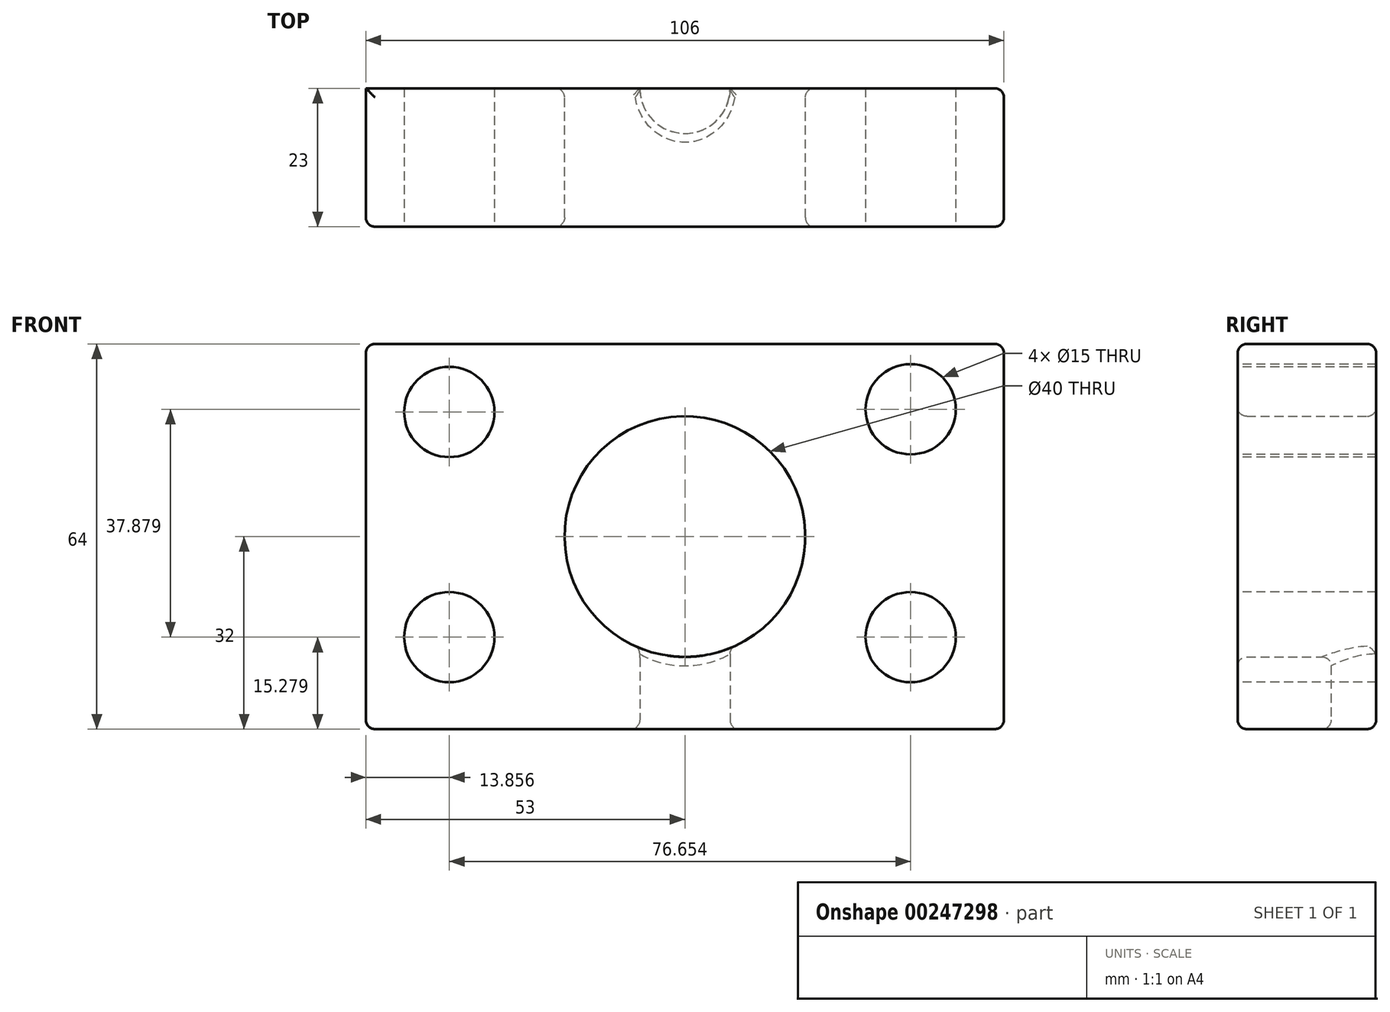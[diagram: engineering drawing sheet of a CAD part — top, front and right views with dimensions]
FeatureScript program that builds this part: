
annotation { "Feature Type Name" : "Feature", "Feature Type Description" : "" }
export const myFeature = defineFeature(function(context is Context, id is Id, definition is map)
    precondition{}
    {
        {
            var Q0;
            Q0=qCreatedBy(makeId("Front.planeOp"),FACE);
            var sketch = newSketch(context, id + "F0", { "sketchPlane" : qUnion([Q0])});
            skCircle(sketch, "E0", {"center": v(0, 0) * mm, "radius": 20 * mm});
            skLineSegment(sketch, "E1.bottom", {"start": v(-53, 32) * mm, "end": v(53, 32) * mm});
            skLineSegment(sketch, "E1.top", {"start": v(-53, -32) * mm, "end": v(53, -32) * mm});
            skLineSegment(sketch, "E1.left", {"start": v(-53, 32) * mm, "end": v(-53, -32) * mm});
            skLineSegment(sketch, "E1.right", {"start": v(53, 32) * mm, "end": v(53, -32) * mm});
            skSolve(sketch);
        }
        {
            var Q0;
            Q0=makeQuery(id+"F0.imprint","IMPRINT",FACE,{"disambiguationData":[TD([[makeQuery(id+"F0.imprint","IMPRINT",EDGE,{"derivedFrom":sQuery(id+"F0.wireOp",EDGE,"E0")}),-1.0]])]});
            extrude(context, id + "F1", {"entities" : qUnion([Q0]), "depth" : 23 * mm});
        }
        {
            var Q0;
            Q0=makeQuery(id+"F1.opExtrude","SWEPT_FACE",FACE,{"disambiguationData":[OSD([sQuery(id+"F0.wireOp",EDGE,"E1.top")])]});
            var sketch = newSketch(context, id + "F2", { "sketchPlane" : qUnion([Q0])});
            skArc(sketch, "E2", {"start": v(7.5, 0) * mm, "mid": v(0, 7.5) * mm, "end": v(-7.5, 0) * mm});
            skSolve(sketch);
        }
        {
            var Q0;
            Q0=qSketchRegion(id+"F2",true);
            var Q1;
            {var subQ0=sQuery(id+"F2.wireOp",EDGE,"E2");Q1=makeQuery(id+"F2.imprint","IMPRINT",FACE,{"disambiguationData":[TD([[makeQuery(id+"F2.imprint","IMPRINT",EDGE,{"derivedFrom":subQ0}),1.0]])]});}
            extrude(context, id + "F3", {"entities" : qUnion([Q0, Q1]), "operationType" : NewBodyOperationType.REMOVE, "oppositeDirection" : true, "depth" : 25 * mm});
        }
        {
            var Q0;
            Q0=makeQuery(id+"F1.opExtrude","SWEPT_FACE",FACE,{"disambiguationData":[OSD([sQuery(id+"F0.wireOp",EDGE,"E1.top")])]});
            var Q1;
            Q1=makeQuery(id+"F1.opExtrude","CAP_FACE",FACE,{"disambiguationData":[OSD([sQuery(id+"F0.wireOp",EDGE,"E0"),sQuery(id+"F0.wireOp",EDGE,"E1.bottom"),sQuery(id+"F0.wireOp",EDGE,"E1.top"),sQuery(id+"F0.wireOp",EDGE,"E1.left"),sQuery(id+"F0.wireOp",EDGE,"E1.right")])],"isStart":false});
            var Q2;
            Q2=makeQuery(id+"F1.opExtrude","SWEPT_FACE",FACE,{"disambiguationData":[OSD([sQuery(id+"F0.wireOp",EDGE,"E1.right")])]});
            var Q3;
            Q3=makeQuery(id+"F1.opExtrude","SWEPT_FACE",FACE,{"disambiguationData":[OSD([sQuery(id+"F0.wireOp",EDGE,"E1.bottom")])]});
            var Q4;
            Q4=makeQuery(id+"F1.opExtrude","CAP_EDGE",EDGE,{"disambiguationData":[OSD([sQuery(id+"F0.wireOp",EDGE,"E0")])],"isStart":true});
            var Q5;
            {var subQ0=sQuery(id+"F2.wireOp",EDGE,"E2");var subQ1=sQuery(id+"F0.wireOp",EDGE,"E1.top");Q5=makeQuery(id+"F3.boolean.opBoolean","COPY",EDGE,{"derivedFrom":makeQuery(id+"F3.opExtrude","SWEPT_EDGE",EDGE,{"disambiguationData":[OSD([subQ1,subQ0]),TDD([makeQuery(id+"F2.imprint","INTERSECT",VERTEX,{"disambiguationData":[OD(0.0)],"derivedFrom":[makeQuery(id+"F1.opExtrude","CAP_EDGE",EDGE,{"disambiguationData":[OSD([subQ1])],"isStart":true}),subQ0]})])]})});}
            var Q6;
            {var subQ0=sQuery(id+"F2.wireOp",EDGE,"E2");var subQ1=sQuery(id+"F0.wireOp",EDGE,"E1.top");Q6=makeQuery(id+"F3.boolean.opBoolean","COPY",EDGE,{"derivedFrom":makeQuery(id+"F3.opExtrude","SWEPT_EDGE",EDGE,{"disambiguationData":[OSD([subQ1,subQ0]),TDD([makeQuery(id+"F2.imprint","INTERSECT",VERTEX,{"disambiguationData":[OD(1.0)],"derivedFrom":[makeQuery(id+"F1.opExtrude","CAP_EDGE",EDGE,{"disambiguationData":[OSD([subQ1])],"isStart":true}),subQ0]})])]})});}
            var Q7;
            Q7=makeQuery(id+"F3.boolean.opBoolean","INTERSECT",EDGE,{"derivedFrom":[makeQuery(id+"F1.opExtrude","SWEPT_FACE",FACE,{"disambiguationData":[OSD([sQuery(id+"F0.wireOp",EDGE,"E0")])]}),makeQuery(id+"F3.opExtrude","SWEPT_FACE",FACE,{"disambiguationData":[OSD([sQuery(id+"F2.wireOp",EDGE,"E2")])]})]});
            fillet(context, id + "F4", {"entities" : qUnion([Q0, Q1, Q2, Q3, Q4, Q5, Q6, Q7]), "radius" : 1.5 * mm, "tangentPropagation" : true, "allowEdgeOverflow" : false});
        }
        {
            var Q0;
            Q0=makeQuery(id+"F1.opExtrude","CAP_FACE",FACE,{"disambiguationData":[OSD([sQuery(id+"F0.wireOp",EDGE,"E0"),sQuery(id+"F0.wireOp",EDGE,"E1.bottom"),sQuery(id+"F0.wireOp",EDGE,"E1.top"),sQuery(id+"F0.wireOp",EDGE,"E1.left"),sQuery(id+"F0.wireOp",EDGE,"E1.right")])],"isStart":false});
            var sketch = newSketch(context, id + "F5", { "sketchPlane" : qUnion([Q0])});
            skPoint(sketch, "E3", {"position": v(-39.14, 20.7) * mm});
            skPoint(sketch, "E4", {"position": v(37.5, 21.16) * mm});
            skPoint(sketch, "E5", {"position": v(37.5, -16.72) * mm});
            skPoint(sketch, "E6", {"position": v(-39.14, -16.72) * mm});
            skSolve(sketch);
        }
        {
            var Q0;
            Q0=sQuery(id+"F5.wireOp",VERTEX,"E3");
            var Q1;
            Q1=sQuery(id+"F5.wireOp",VERTEX,"E4");
            var Q2;
            Q2=sQuery(id+"F5.wireOp",VERTEX,"E5");
            var Q3;
            Q3=sQuery(id+"F5.wireOp",VERTEX,"E6");
            var Q4;
            Q4=makeQuery(id+"F1.opExtrude","SWEPT_BODY",BODY,{"disambiguationData":[OSD([sQuery(id+"F0.wireOp",EDGE,"E0"),sQuery(id+"F0.wireOp",EDGE,"E1.bottom"),sQuery(id+"F0.wireOp",EDGE,"E1.top"),sQuery(id+"F0.wireOp",EDGE,"E1.left"),sQuery(id+"F0.wireOp",EDGE,"E1.right")])]});
            hole(context, id + "F6", {"style" : HoleStyle.SIMPLE, "endStyle" : HoleEndStyle.THROUGH, "holeDiameter" : 15 * mm, "startFromSketch" : true, "locations" : qUnion([Q0, Q1, Q2, Q3]), "scope" : qUnion([Q4]), "isTappedThrough" : true});
        }
    });
